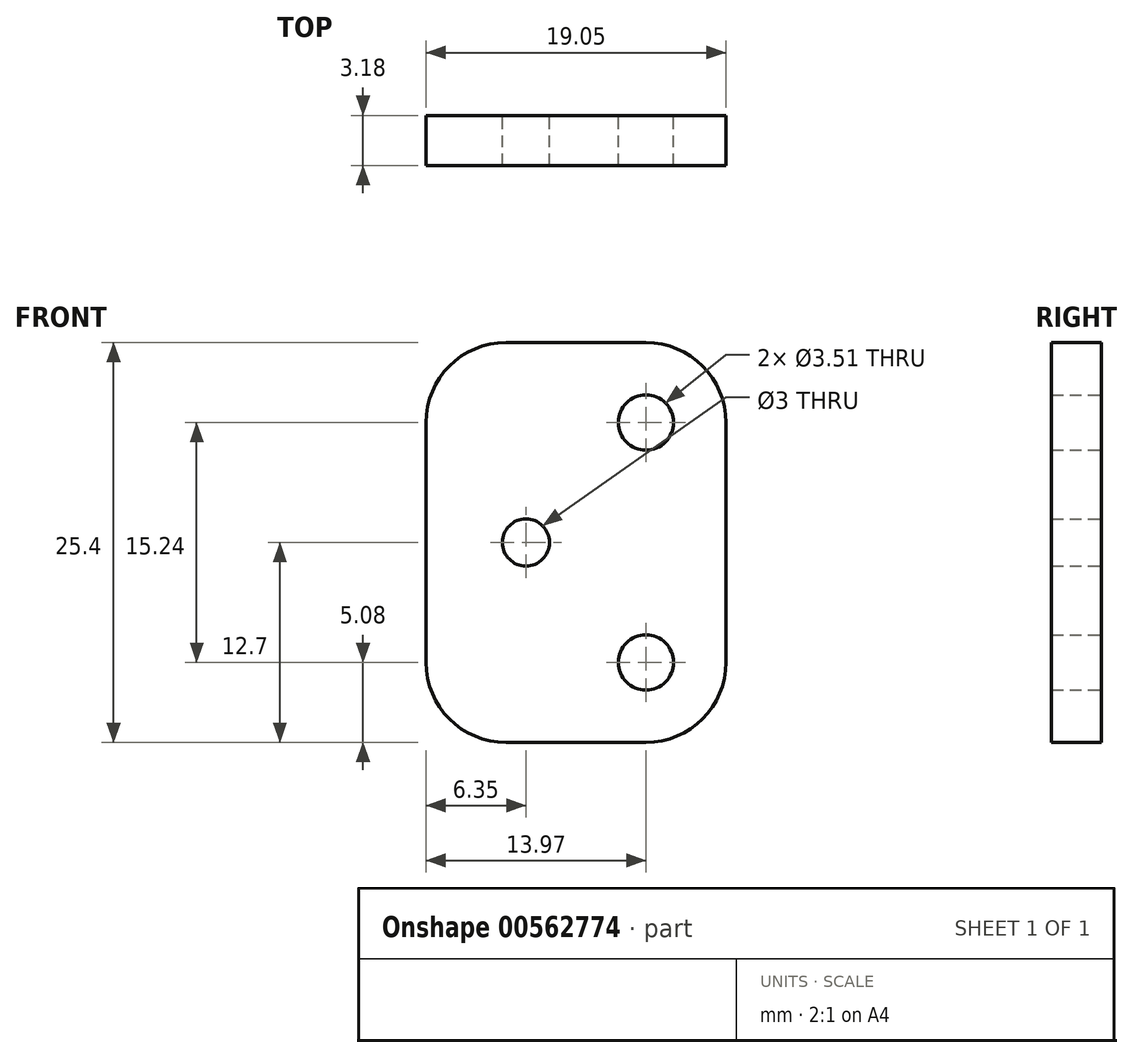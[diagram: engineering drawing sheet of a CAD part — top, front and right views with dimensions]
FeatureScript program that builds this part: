
annotation { "Feature Type Name" : "Feature", "Feature Type Description" : "" }
export const myFeature = defineFeature(function(context is Context, id is Id, definition is map)
    precondition{}
    {
        {
            var Q0;
            Q0=qCreatedBy(makeId("Front.planeOp"),FACE);
            var sketch = newSketch(context, id + "F0", { "sketchPlane" : qUnion([Q0])});
            skLineSegment(sketch, "E0.bottom", {"start": v(-6.35, 12.7) * mm, "end": v(12.7, 12.7) * mm});
            skLineSegment(sketch, "E0.top", {"start": v(-6.35, -12.7) * mm, "end": v(12.7, -12.7) * mm});
            skLineSegment(sketch, "E0.right", {"start": v(12.7, 12.7) * mm, "end": v(12.7, -12.7) * mm});
            skPoint(sketch, "E0.middle", {"position": v(0, 0) * mm});
            skCircle(sketch, "E1", {"center": v(0, 0) * mm, "radius": 1.5 * mm});
            skCircle(sketch, "E2", {"center": v(7.62, 7.62) * mm, "radius": 1.75 * mm});
            skCircle(sketch, "E3.MirrorC", {"center": v(7.62, -7.62) * mm, "radius": 1.75 * mm});
            skLineSegment(sketch, "E4", {"start": v(-6.35, 12.7) * mm, "end": v(-6.35, -12.7) * mm});
            skPoint(sketch, "E0.left.start.orphan", {"position": v(-12.7, 12.7) * mm});
            skPoint(sketch, "E5.orphan", {"position": v(-12.7, -12.7) * mm});
            skSolve(sketch);
        }
        {
            var Q0;
            Q0 = qSketchRegion(id + "F0", true);
            extrude(context, id + "F1", {"entities" : qUnion([Q0]), "depth" : 3.17 * mm, "offsetDistance" : 25.4 * mm});
        }
        {
            var Q0;
            Q0=makeQuery(id+"F1.opExtrude","SWEPT_EDGE",EDGE,{"disambiguationData":[OSD([sQuery(id+"F0.wireOp",EDGE,"E0.bottom"),sQuery(id+"F0.wireOp",EDGE,"E0.left")])]});
            var Q1;
            Q1=makeQuery(id+"F1.opExtrude","SWEPT_EDGE",EDGE,{"disambiguationData":[OSD([sQuery(id+"F0.wireOp",EDGE,"E0.top"),sQuery(id+"F0.wireOp",EDGE,"E0.left")])]});
            var Q2;
            Q2=makeQuery(id+"F1.opExtrude","SWEPT_EDGE",EDGE,{"disambiguationData":[OSD([sQuery(id+"F0.wireOp",EDGE,"E0.bottom"),sQuery(id+"F0.wireOp",EDGE,"E0.right")])]});
            var Q3;
            Q3=makeQuery(id+"F1.opExtrude","SWEPT_EDGE",EDGE,{"disambiguationData":[OSD([sQuery(id+"F0.wireOp",EDGE,"E0.top"),sQuery(id+"F0.wireOp",EDGE,"E0.right")])]});
            fillet(context, id + "F2", {"entities" : qUnion([Q0, Q1, Q2, Q3]), "radius" : 5.08 * mm, "tangentPropagation" : true, "allowEdgeOverflow" : false});
        }
    });
